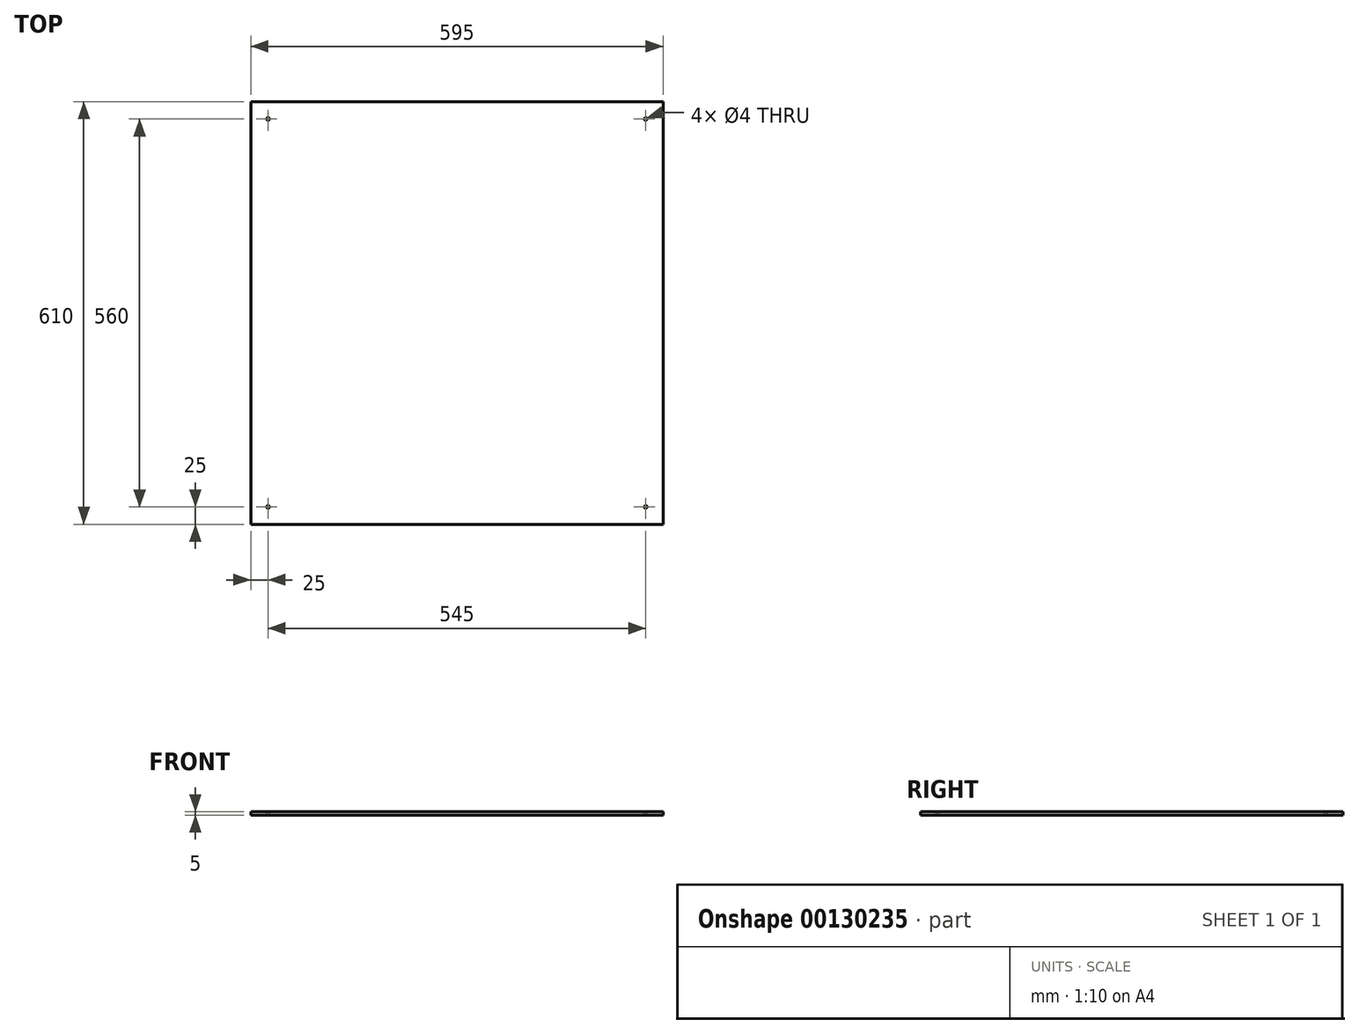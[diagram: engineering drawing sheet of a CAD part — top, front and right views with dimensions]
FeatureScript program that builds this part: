
annotation { "Feature Type Name" : "Feature", "Feature Type Description" : "" }
export const myFeature = defineFeature(function(context is Context, id is Id, definition is map)
    precondition{}
    {
        {
            var Q0;
            Q0=qCreatedBy(makeId("Top.planeOp"),FACE);
            var sketch = newSketch(context, id + "F0", { "sketchPlane" : qUnion([Q0])});
            skLineSegment(sketch, "E0.bottom", {"start": v(-297.5, 305) * mm, "end": v(297.5, 305) * mm});
            skLineSegment(sketch, "E0.top", {"start": v(-297.5, -305) * mm, "end": v(297.5, -305) * mm});
            skLineSegment(sketch, "E0.left", {"start": v(-297.5, 305) * mm, "end": v(-297.5, -305) * mm});
            skLineSegment(sketch, "E0.right", {"start": v(297.5, 305) * mm, "end": v(297.5, -305) * mm});
            skPoint(sketch, "E0.middle", {"position": v(0, 0) * mm});
            skCircle(sketch, "E1", {"center": v(-272.5, 280) * mm, "radius": 2 * mm});
            skCircle(sketch, "E2.MirrorC", {"center": v(272.5, 280) * mm, "radius": 2 * mm});
            skCircle(sketch, "E3.MirrorC", {"center": v(272.5, -280) * mm, "radius": 2 * mm});
            skCircle(sketch, "E4.MirrorC", {"center": v(-272.5, -280) * mm, "radius": 2 * mm});
            skSolve(sketch);
        }
        {
            var Q0;
            Q0=makeQuery(id+"F0.imprint","IMPRINT",FACE,{"disambiguationData":[TD([[makeQuery(id+"F0.imprint","IMPRINT",EDGE,{"derivedFrom":sQuery(id+"F0.wireOp",EDGE,"E0.bottom")}),-1.0]])]});
            extrude(context, id + "F1", {"entities" : qUnion([Q0]), "oppositeDirection" : true, "depth" : 5 * mm});
        }
    });
